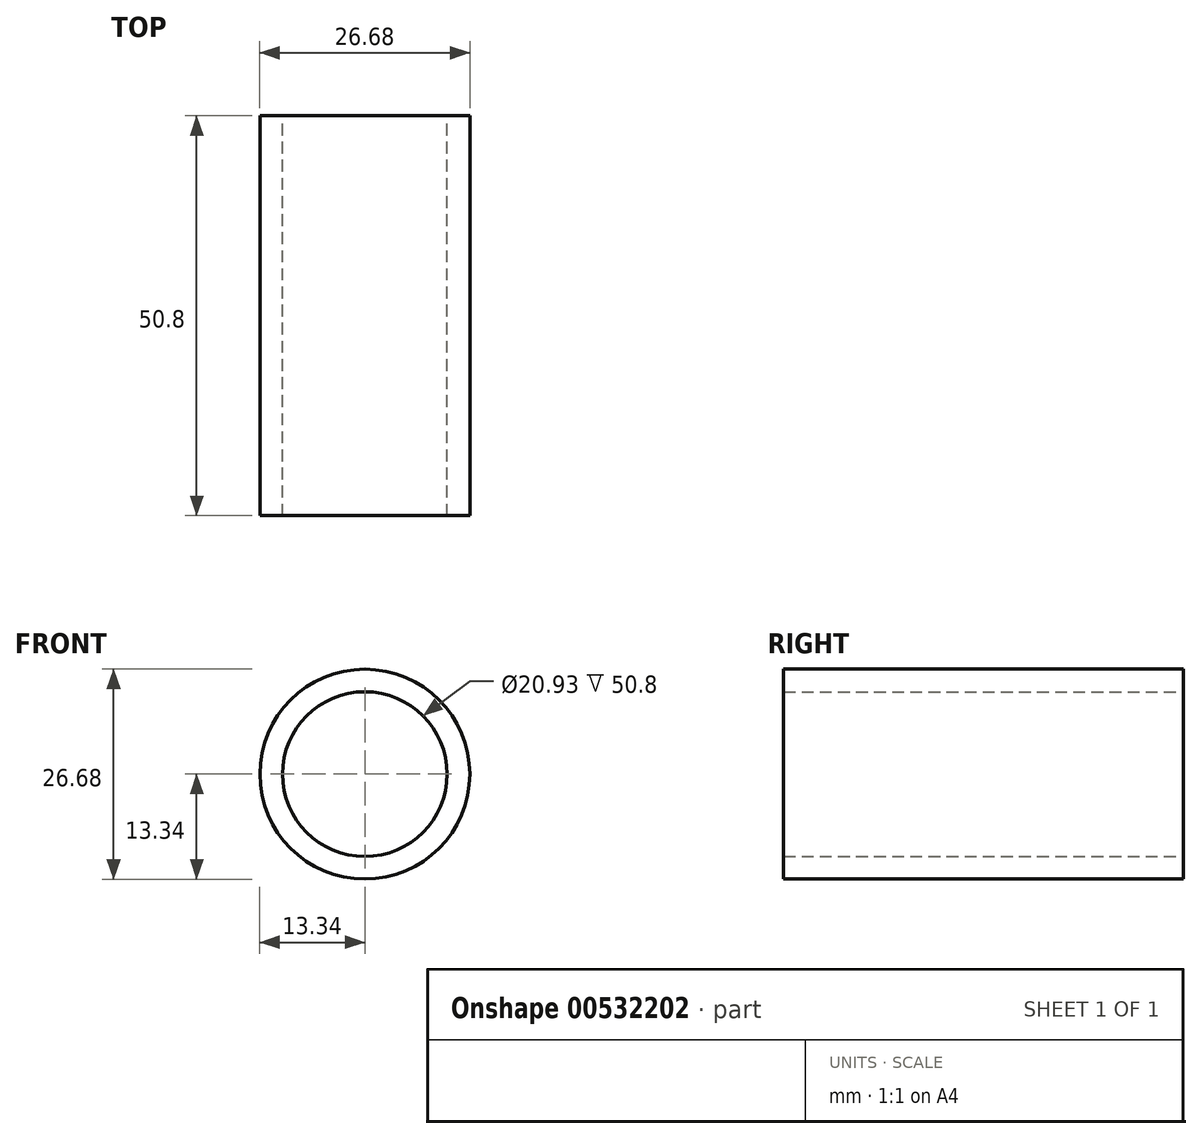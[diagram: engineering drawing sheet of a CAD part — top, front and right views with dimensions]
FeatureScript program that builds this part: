
annotation { "Feature Type Name" : "Feature", "Feature Type Description" : "" }
export const myFeature = defineFeature(function(context is Context, id is Id, definition is map)
    precondition{}
    {
        {
            var Q0;
            Q0=qCreatedBy(makeId("Front.planeOp"),FACE);
            var sketch = newSketch(context, id + "F0", { "sketchPlane" : qUnion([Q0])});
            skCircle(sketch, "E0", {"center": v(0, 0) * mm, "radius": 13.34 * mm});
            skCircle(sketch, "E1", {"center": v(0, 0) * mm, "radius": 10.46 * mm});
            skSolve(sketch);
        }
        {
            var Q0;
            Q0 = qSketchRegion(id + "F0", true);
            extrude(context, id + "F1", {"entities" : qUnion([Q0]), "depth" : 50.8 * mm, "offsetDistance" : 25.4 * mm});
        }
    });
